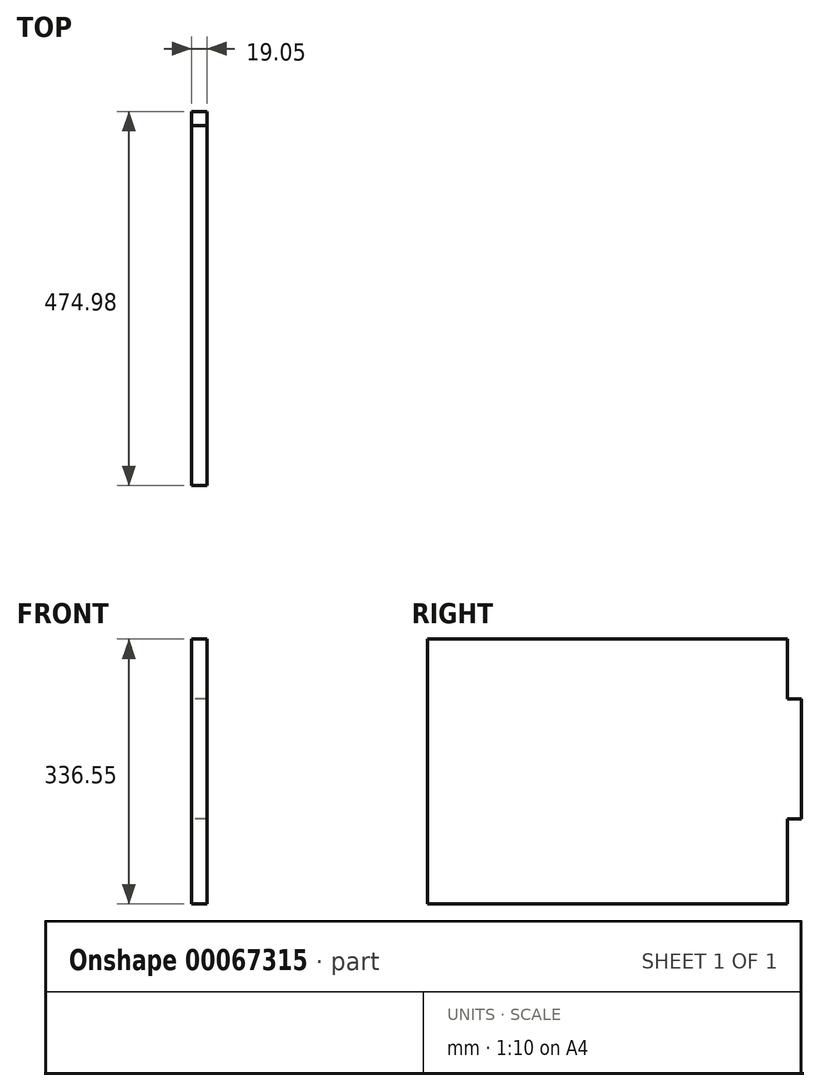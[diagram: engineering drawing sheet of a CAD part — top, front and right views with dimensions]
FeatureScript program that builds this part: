
annotation { "Feature Type Name" : "Feature", "Feature Type Description" : "" }
export const myFeature = defineFeature(function(context is Context, id is Id, definition is map)
    precondition{}
    {
        {
            var Q0;
            Q0=qCreatedBy(makeId("Right.planeOp"),FACE);
            var sketch = newSketch(context, id + "F0", { "sketchPlane" : qUnion([Q0])});
            skLineSegment(sketch, "E0.bottom", {"start": v(-228.6, 0) * mm, "end": v(228.6, 0) * mm});
            skLineSegment(sketch, "E0.top", {"start": v(-228.6, -336.55) * mm, "end": v(228.6, -336.55) * mm});
            skLineSegment(sketch, "E0.left", {"start": v(-228.6, 0) * mm, "end": v(-228.6, -336.55) * mm});
            skLineSegment(sketch, "E0.right", {"start": v(228.6, 0) * mm, "end": v(228.6, -336.55) * mm});
            skLineSegment(sketch, "E1.bottom", {"start": v(-76.2, 0) * mm, "end": v(76.2, 0) * mm});
            skLineSegment(sketch, "E1.top", {"start": v(-76.2, 17.78) * mm, "end": v(76.2, 17.78) * mm});
            skLineSegment(sketch, "E1.left", {"start": v(-76.2, 0) * mm, "end": v(-76.2, 17.78) * mm});
            skLineSegment(sketch, "E1.right", {"start": v(76.2, 0) * mm, "end": v(76.2, 17.78) * mm});
            skLineSegment(sketch, "E2.bottom", {"start": v(228.6, -76.2) * mm, "end": v(246.38, -76.2) * mm});
            skLineSegment(sketch, "E2.top", {"start": v(228.6, -228.6) * mm, "end": v(246.38, -228.6) * mm});
            skLineSegment(sketch, "E2.left", {"start": v(228.6, -76.2) * mm, "end": v(228.6, -228.6) * mm});
            skLineSegment(sketch, "E2.right", {"start": v(246.38, -76.2) * mm, "end": v(246.38, -228.6) * mm});
            skLineSegment(sketch, "E3.bottom", {"start": v(-76.2, -336.55) * mm, "end": v(76.2, -336.55) * mm});
            skLineSegment(sketch, "E3.top", {"start": v(-76.2, -354.33) * mm, "end": v(76.2, -354.33) * mm});
            skLineSegment(sketch, "E3.left", {"start": v(-76.2, -336.55) * mm, "end": v(-76.2, -354.33) * mm});
            skLineSegment(sketch, "E3.right", {"start": v(76.2, -336.55) * mm, "end": v(76.2, -354.33) * mm});
            skSolve(sketch);
        }
        {
            var Q0;
            Q0=makeQuery(id+"F0.imprint","IMPRINT",FACE,{"disambiguationData":[TD([[makeQuery(id+"F0.imprint","IMPRINT",EDGE,{"derivedFrom":sQuery(id+"F0.wireOp",EDGE,"40ecc8d9-ebdb-4f47-8b77-6c8a05ab18c9.bottom")}),1.0]])]});
            var Q1;
            Q1=makeQuery(id+"F0.imprint","IMPRINT",FACE,{"disambiguationData":[TD([[makeQuery(id+"F0.imprint","IMPRINT",EDGE,{"derivedFrom":sQuery(id+"F0.wireOp",EDGE,"E1.bottom")}),1.0]])]});
            var Q2;
            {var subQ4=sQuery(id+"F0.wireOp",EDGE,"E0.left");Q2=makeQuery(id+"F0.imprint","IMPRINT",FACE,{"disambiguationData":[TD([[makeQuery(id+"F0.imprint","IMPRINT",EDGE,{"derivedFrom":subQ4}),1.0]])]});}
            var Q3;
            Q3=makeQuery(id+"F0.imprint","IMPRINT",FACE,{"disambiguationData":[TD([[makeQuery(id+"F0.imprint","IMPRINT",EDGE,{"derivedFrom":sQuery(id+"F0.wireOp",EDGE,"E2.bottom")}),-1.0]])]});
            var Q4;
            Q4=makeQuery(id+"F0.imprint","IMPRINT",FACE,{"disambiguationData":[TD([[makeQuery(id+"F0.imprint","IMPRINT",EDGE,{"derivedFrom":sQuery(id+"F0.wireOp",EDGE,"E3.bottom")}),-1.0]])]});
            extrude(context, id + "F1", {"entities" : qUnion([Q0, Q1, Q2, Q3, Q4]), "depth" : 19.05 * mm});
        }
    });
